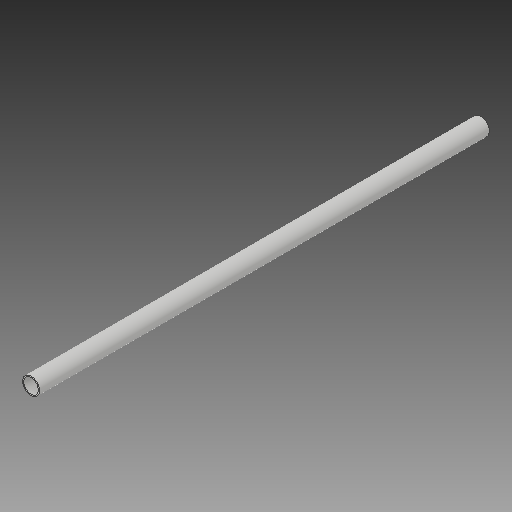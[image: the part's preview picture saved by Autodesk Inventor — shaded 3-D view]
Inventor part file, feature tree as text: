
AUTODESK INVENTOR PART (.ipt)
format: ipt  version: 2018.2 (Build 222227000, 227)  size: 79,872 bytes
history: native  units: mm
features: other x1, extrude x1, sketch x1
ambient origin geometry x8: Origin, YZ Plane, XZ Plane, XY Plane, X Axis, Y Axis, Z Axis, Center Point
bodies: Body1 (feature_tree)
feature tree (3):
  other  "ソリッド1"
  extrude  "押し出し1"  Depth=16.0mm
  sketch  "スケッチ1"
